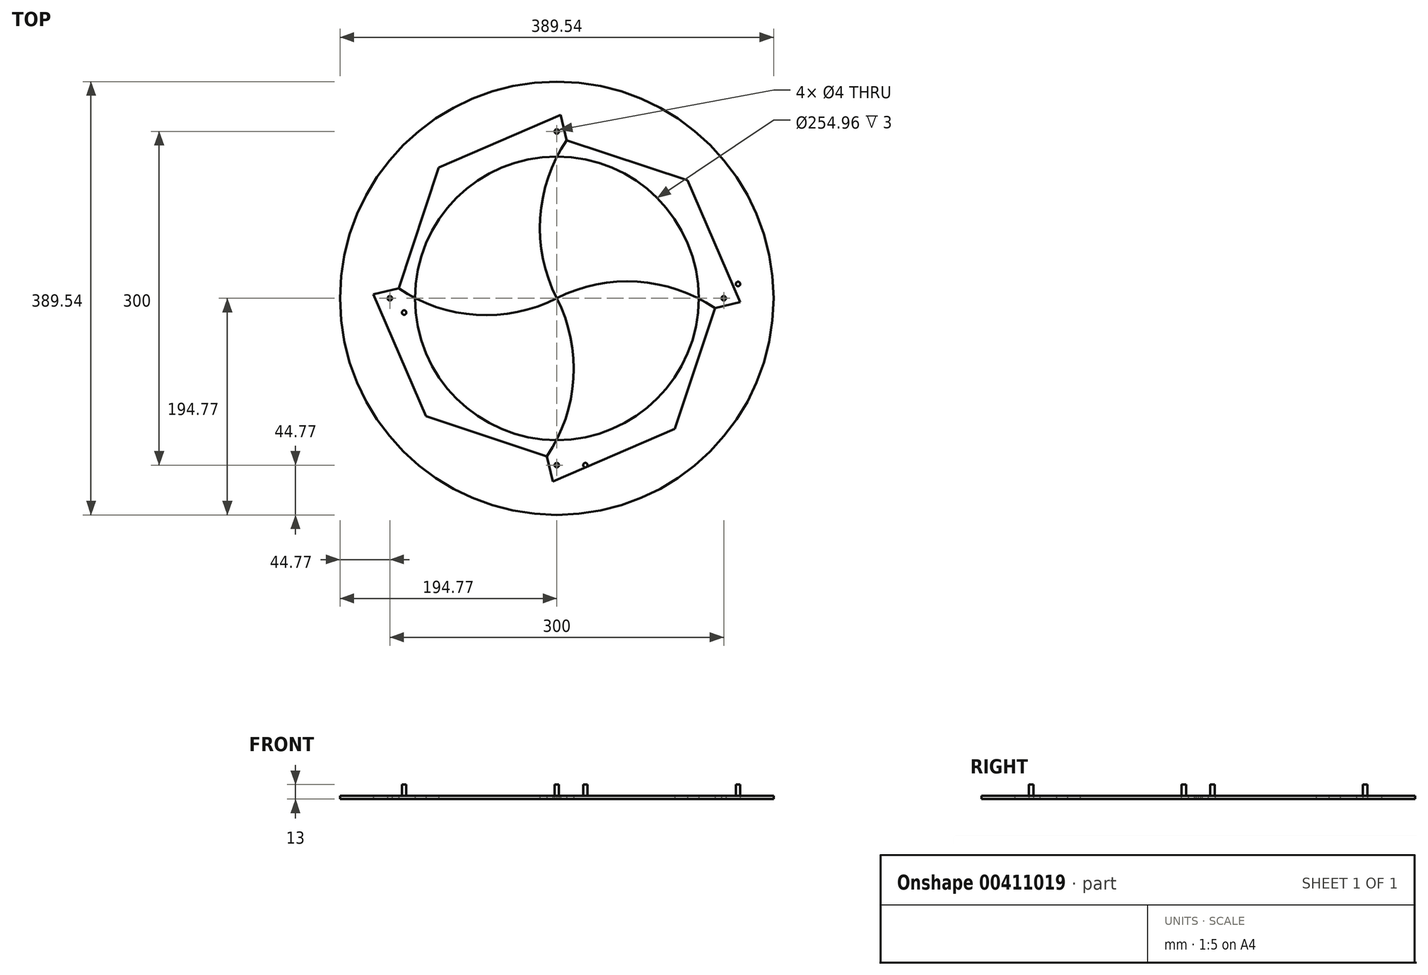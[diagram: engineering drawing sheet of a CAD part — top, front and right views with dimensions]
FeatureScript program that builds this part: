
annotation { "Feature Type Name" : "Feature", "Feature Type Description" : "" }
export const myFeature = defineFeature(function(context is Context, id is Id, definition is map)
    precondition{}
    {
        {
            var Q0;
            Q0=qCreatedBy(makeId("Top.planeOp"),FACE);
            var sketch = newSketch(context, id + "F0", { "sketchPlane" : qUnion([Q0])});
            skCircle(sketch, "E0", {"center": v(0, 0) * mm, "radius": 194.77 * mm});
            skCircle(sketch, "E1", {"center": v(0, 0) * mm, "radius": 127.48 * mm});
            skSolve(sketch);
        }
        {
            var Q0;
            Q0=makeQuery(id+"F0.imprint","IMPRINT",FACE,{"disambiguationData":[TD([[makeQuery(id+"F0.imprint","IMPRINT",EDGE,{"derivedFrom":sQuery(id+"F0.wireOp",EDGE,"E0")}),1.0]])]});
            extrude(context, id + "F1", {"entities" : qUnion([Q0]), "depth" : 3 * mm});
        }
        {
            var Q0;
            Q0=makeQuery(id+"F1.opExtrude","CAP_FACE",FACE,{"disambiguationData":[OSD([sQuery(id+"F0.wireOp",EDGE,"E0"),sQuery(id+"F0.wireOp",EDGE,"E1")])],"isStart":false});
            var sketch = newSketch(context, id + "F2", { "sketchPlane" : qUnion([Q0])});
            skSolve(sketch);
        }
        {
            var Q0;
            Q0=makeQuery(id+"F2.imprint","IMPRINT",FACE,{"disambiguationData":[TD([[makeQuery(id+"F2.imprint","IMPRINT",EDGE,{"derivedFrom":makeQuery(id+"F1.opExtrude","CAP_EDGE",EDGE,{"disambiguationData":[OSD([sQuery(id+"F0.wireOp",EDGE,"E0")])],"isStart":false})}),1.0]])]});
            var sketch = newSketch(context, id + "F3", { "sketchPlane" : qUnion([Q0])});
            skCircle(sketch, "E2", {"center": v(0, 150) * mm, "radius": 2 * mm});
            skCircle(sketch, "E3.1.0", {"center": v(-137.15, -12.85) * mm, "radius": 2 * mm});
            skCircle(sketch, "E3.2.0", {"center": v(25.7, -150) * mm, "radius": 2 * mm});
            skCircle(sketch, "E3.3.0", {"center": v(162.85, 12.85) * mm, "radius": 2 * mm});
            skPoint(sketch, "E3.center", {"position": v(12.85, 0) * mm});
            skSolve(sketch);
        }
        {
            var Q0;
            Q0=qSketchRegion(id+"F3",true);
            extrude(context, id + "F4", {"entities" : qUnion([Q0]), "operationType" : NewBodyOperationType.ADD, "depth" : 10 * mm});
        }
        {
            var Q0;
            Q0=qCreatedBy(makeId("Top.planeOp"),FACE);
            var sketch = newSketch(context, id + "F5", { "sketchPlane" : qUnion([Q0])});
            skArc(sketch, "E4", {"start": v(8.93, 142.12) * mm, "mid": v(-14.94, 72.28) * mm, "end": v(0, 0) * mm});
            skPoint(sketch, "E5.center", {"position": v(0, 0) * mm});
            skCircle(sketch, "E6.0", {"center": v(0, 150) * mm, "radius": 2 * mm});
            skArc(sketch, "E7.1.0", {"start": v(-142.12, 8.93) * mm, "mid": v(-72.28, -14.94) * mm, "end": v(0, 0) * mm});
            skLineSegment(sketch, "E8", {"start": v(8.93, 142.12) * mm, "end": v(3.45, 164.78) * mm});
            skLineSegment(sketch, "E9", {"start": v(3.45, 164.78) * mm, "end": v(-106.09, 117.5) * mm});
            skLineSegment(sketch, "E10", {"start": v(-106.09, 117.5) * mm, "end": v(-142.12, 8.93) * mm});
            skSolve(sketch);
        }
        {
            var Q0;
            Q0 = qSketchRegion(id + "F5", true);
            extrude(context, id + "F6", {"entities" : qUnion([Q0]), "depth" : 3 * mm});
        }
        {
            var Q0;
            Q0=makeQuery(id+"F6.opExtrude","SWEPT_BODY",BODY,{"disambiguationData":[OSD([sQuery(id+"F5.wireOp",EDGE,"E4"),sQuery(id+"F5.wireOp",EDGE,"E5.14.0"),sQuery(id+"F5.wireOp",EDGE,"daqgzb58-1Qsf-domH-fy6u-O6Z0h6G8pY7R"),sQuery(id+"F5.wireOp",EDGE,"881e4rIN-yicR-qTvN-inSL-3wopSEfX8S8y"),sQuery(id+"F5.wireOp",EDGE,"E6.0")])]});
            var Q1;
            Q1=makeQuery(id+"F1.opExtrude","CAP_EDGE",EDGE,{"disambiguationData":[OSD([sQuery(id+"F0.wireOp",EDGE,"E1")])],"isStart":false});
            circularPattern(context, id + "F7", {"entities" : qUnion([Q0]), "axis" : qUnion([Q1]), "angle" : 360 * degree, "instanceCount" : 4, "equalSpace" : true});
        }
    });
